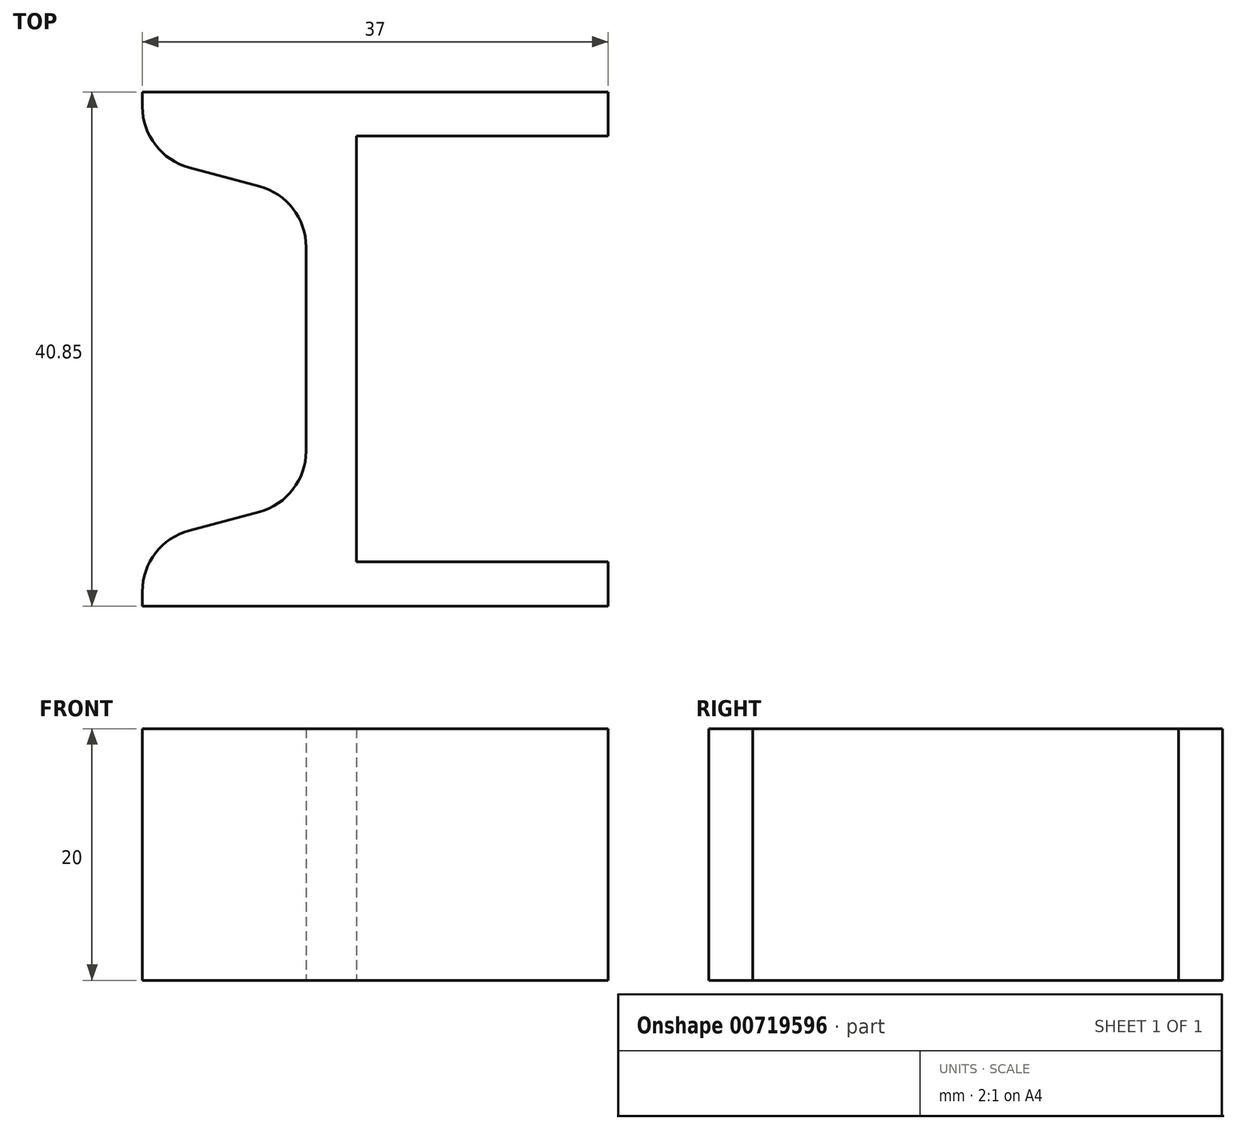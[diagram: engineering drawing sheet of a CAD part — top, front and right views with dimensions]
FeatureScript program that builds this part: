
annotation { "Feature Type Name" : "Feature", "Feature Type Description" : "" }
export const myFeature = defineFeature(function(context is Context, id is Id, definition is map)
    precondition{}
    {
        {
            var Q0;
            Q0=qCreatedBy(makeId("Top.planeOp"),FACE);
            var sketch = newSketch(context, id + "F0", { "sketchPlane" : qUnion([Q0])});
            skLineSegment(sketch, "E0", {"start": v(20, 0) * mm, "end": v(0, 0) * mm});
            skLineSegment(sketch, "E1", {"start": v(0, 0) * mm, "end": v(0, 33.85) * mm});
            skLineSegment(sketch, "E2", {"start": v(0, 33.85) * mm, "end": v(20, 33.85) * mm});
            skLineSegment(sketch, "E3", {"start": v(-17, 37.35) * mm, "end": v(-17, -3.5) * mm, "construction": true});
            skLineSegment(sketch, "E4", {"start": v(20, 37.35) * mm, "end": v(-17, 37.35) * mm});
            skLineSegment(sketch, "E5", {"start": v(-17, -3.5) * mm, "end": v(20, -3.5) * mm});
            skLineSegment(sketch, "E6", {"start": v(0, 16.93) * mm, "end": v(-17, 16.92) * mm, "construction": true});
            skLineSegment(sketch, "E7", {"start": v(-13.3, 31.36) * mm, "end": v(-7.7, 29.86) * mm});
            skLineSegment(sketch, "E8", {"start": v(-4, 25.03) * mm, "end": v(-4, 16.93) * mm});
            skLineSegment(sketch, "E9", {"start": v(-17, 36.19) * mm, "end": v(-17, 37.35) * mm});
            skPoint(sketch, "E10.visualSharp", {"position": v(-17, 32.35) * mm});
            skArc(sketch, "E10.filletArc", {"start": v(-17, 36.19) * mm, "mid": v(-15.97, 33.14) * mm, "end": v(-13.3, 31.36) * mm});
            skPoint(sketch, "E11.visualSharp", {"position": v(-4, 28.87) * mm});
            skArc(sketch, "E11.filletArc", {"start": v(-4, 25.03) * mm, "mid": v(-5.03, 28.07) * mm, "end": v(-7.7, 29.86) * mm});
            skLineSegment(sketch, "E12.MirrorCS", {"start": v(-4, 8.82) * mm, "end": v(-4, 16.93) * mm});
            skArc(sketch, "E13.MirrorCS", {"start": v(-4, 8.82) * mm, "mid": v(-5.03, 5.78) * mm, "end": v(-7.7, 4) * mm});
            skLineSegment(sketch, "E14.MirrorCS", {"start": v(-13.3, 2.5) * mm, "end": v(-7.7, 4) * mm});
            skArc(sketch, "E15.MirrorCS", {"start": v(-17, -2.34) * mm, "mid": v(-15.97, 0.7) * mm, "end": v(-13.3, 2.5) * mm});
            skLineSegment(sketch, "E16", {"start": v(-17, -2.34) * mm, "end": v(-17, -3.5) * mm});
            skLineSegment(sketch, "E17", {"start": v(20, 37.35) * mm, "end": v(20, 33.85) * mm});
            skLineSegment(sketch, "E18", {"start": v(20, 0) * mm, "end": v(20, -3.5) * mm});
            skSolve(sketch);
        }
        {
            var Q0;
            Q0=makeQuery(id+"F0.imprint","IMPRINT",FACE,{"disambiguationData":[TD([[makeQuery(id+"F0.imprint","IMPRINT",EDGE,{"derivedFrom":sQuery(id+"F0.wireOp",EDGE,"E0")}),1.0]])]});
            extrude(context, id + "F1", {"entities" : qUnion([Q0]), "depth" : 20 * mm, "offsetDistance" : 25 * mm});
        }
    });
